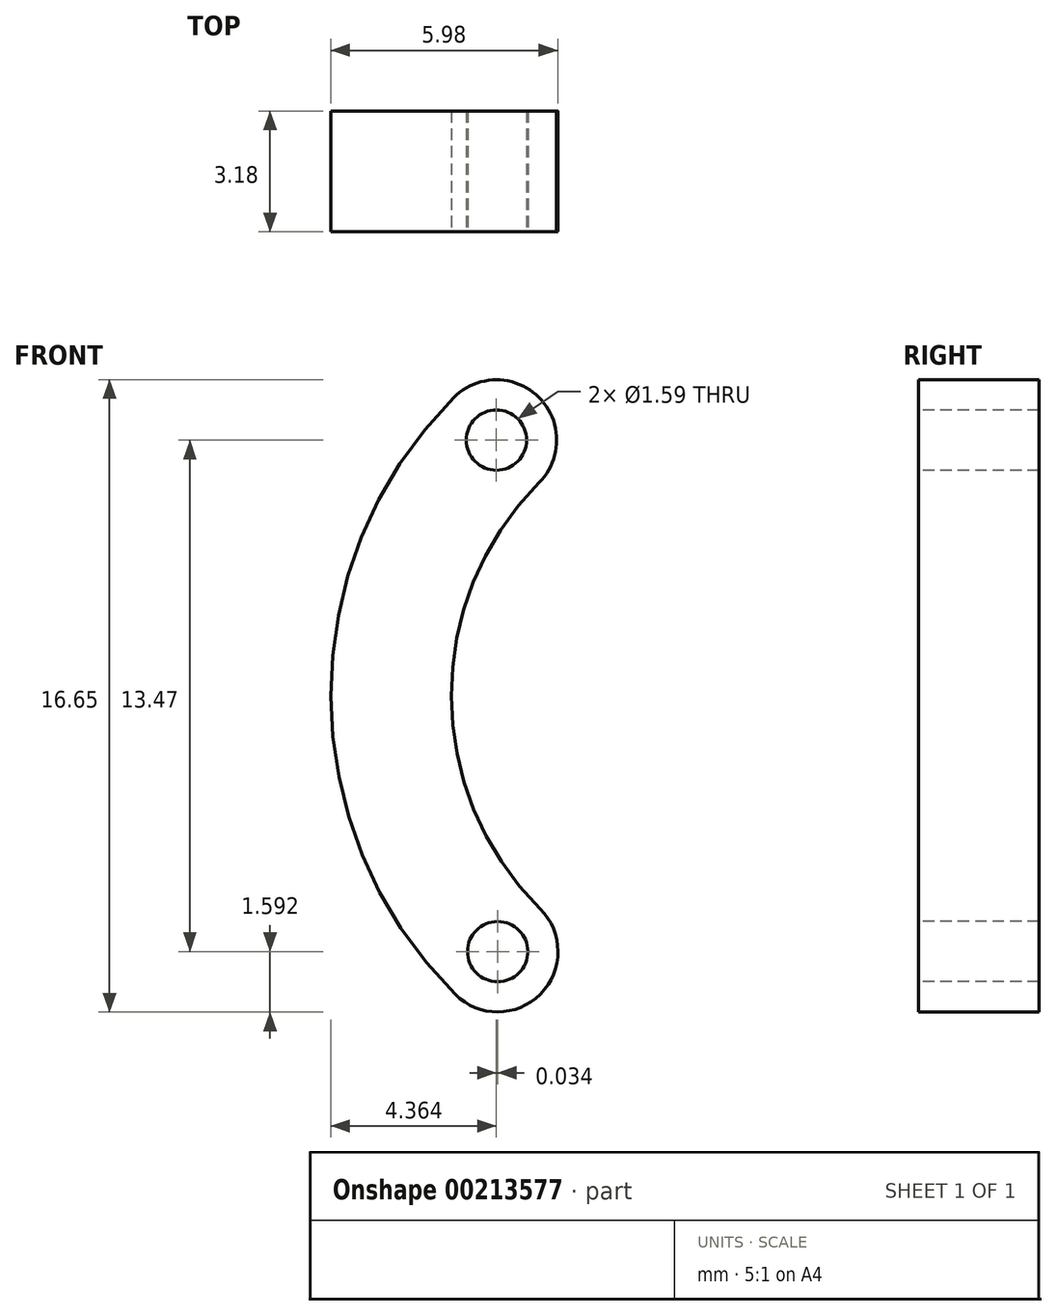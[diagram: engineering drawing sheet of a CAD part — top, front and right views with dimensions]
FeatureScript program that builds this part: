
annotation { "Feature Type Name" : "Feature", "Feature Type Description" : "" }
export const myFeature = defineFeature(function(context is Context, id is Id, definition is map)
    precondition{}
    {
        {
            var Q0;
            Q0=qCreatedBy(makeId("Front.planeOp"),FACE);
            var sketch = newSketch(context, id + "F0", { "sketchPlane" : qUnion([Q0])});
            skCircle(sketch, "E0", {"center": v(1.6, 0.06) * mm, "radius": 7.94 * mm});
            skCircle(sketch, "E1", {"center": v(1.6, 0.06) * mm, "radius": 11.11 * mm});
            skLineSegment(sketch, "E2", {"start": v(1.6, 15.67) * mm, "end": v(1.6, -17.3) * mm, "construction": true});
            skLineSegment(sketch, "E3", {"start": v(-12.8, 0.06) * mm, "end": v(17.58, 0.06) * mm, "construction": true});
            skCircle(sketch, "E4", {"center": v(1.6, 0.06) * mm, "radius": 9.53 * mm, "construction": true});
            skLineSegment(sketch, "E5", {"start": v(1.6, 0.06) * mm, "end": v(-9.4, 11) * mm, "construction": true});
            skLineSegment(sketch, "E6", {"start": v(1.6, 0.06) * mm, "end": v(-9.22, -10.82) * mm, "construction": true});
            skLineSegment(sketch, "E7", {"start": v(1.6, 0.06) * mm, "end": v(11.6, -9.87) * mm, "construction": true});
            skLineSegment(sketch, "E8", {"start": v(1.6, 0.06) * mm, "end": v(11.16, 9.67) * mm, "construction": true});
            skCircle(sketch, "E9", {"center": v(1.6, 9.59) * mm, "radius": 0.8 * mm});
            skCircle(sketch, "E10", {"center": v(-5.15, 6.78) * mm, "radius": 0.8 * mm});
            skCircle(sketch, "E11", {"center": v(-5.11, -6.69) * mm, "radius": 0.8 * mm});
            skCircle(sketch, "E12", {"center": v(1.6, -9.46) * mm, "radius": 0.8 * mm});
            skCircle(sketch, "E13", {"center": v(1.6, 9.59) * mm, "radius": 1.59 * mm});
            skCircle(sketch, "E14", {"center": v(-5.15, 6.78) * mm, "radius": 1.59 * mm});
            skCircle(sketch, "E15", {"center": v(-5.11, -6.69) * mm, "radius": 1.59 * mm});
            skCircle(sketch, "E16", {"center": v(1.6, -9.46) * mm, "radius": 1.59 * mm});
            skSolve(sketch);
        }
        {
            var Q0;
            {var subQ0=sQuery(id+"F0.wireOp",EDGE,"E14");var subQ1=sQuery(id+"F0.wireOp",EDGE,"E0");var subQ2=makeQuery(id+"F0.imprint","INTERSECT",VERTEX,{"derivedFrom":[subQ1,subQ0]});Q0=makeQuery(id+"F0.imprint","IMPRINT",FACE,{"disambiguationData":[TD([[makeQuery(id+"F0.imprint","IMPRINT",EDGE,{"disambiguationData":[TD([[subQ2,-1.0]])],"derivedFrom":subQ1}),-1.0]])]});}
            var Q1;
            Q1=makeQuery(id+"F0.imprint","IMPRINT",FACE,{"disambiguationData":[TD([[makeQuery(id+"F0.imprint","IMPRINT",EDGE,{"derivedFrom":sQuery(id+"F0.wireOp",EDGE,"E10")}),-1.0]])]});
            var Q2;
            Q2=makeQuery(id+"F0.imprint","IMPRINT",FACE,{"disambiguationData":[TD([[makeQuery(id+"F0.imprint","IMPRINT",EDGE,{"derivedFrom":sQuery(id+"F0.wireOp",EDGE,"E11")}),-1.0]])]});
            extrude(context, id + "F1", {"entities" : qUnion([Q0, Q1, Q2]), "oppositeDirection" : true, "depth" : 3.17 * mm});
        }
    });
